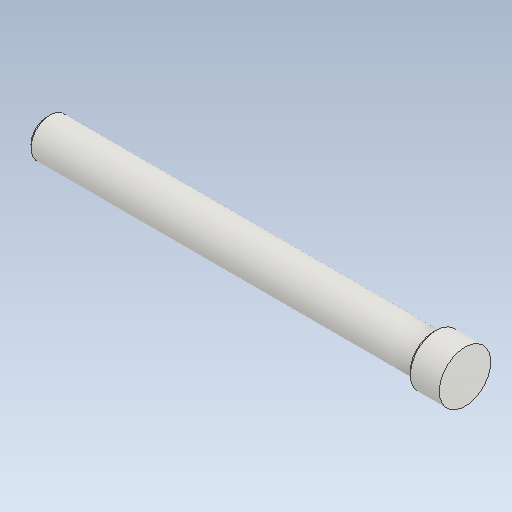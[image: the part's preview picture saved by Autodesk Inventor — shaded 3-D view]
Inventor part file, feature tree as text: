
AUTODESK INVENTOR PART (.ipt)
format: ipt  version: 2020 (Build 240168000, 168)  size: 99,328 bytes
history: native  units: mm
features: other x3, chamfer x2, revolve x1
ambient origin geometry x6: Origin, XZ Plane, XY Plane, X Axis, Y Axis, Z Axis
bodies: Solid1 (feature_tree)
feature tree (6):
  revolve  "Revolution1"  [1 undecoded]
  chamfer  "Chamfer1"  [1 undecoded]
  chamfer  "Chamfer2"  [1 undecoded]
  other  "Start Plane"
  other  "Origin point"
  other  "Main Sketch"
note: 3 required parameter values undecoded (feature->parameter linkage not recoverable at this tier; creation-order binding heuristic only, values carry confidence <= 0.55)